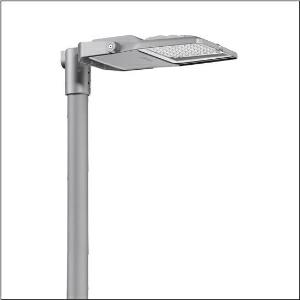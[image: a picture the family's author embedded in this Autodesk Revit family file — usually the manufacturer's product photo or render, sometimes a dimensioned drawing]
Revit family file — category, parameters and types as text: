
# Revit family: floodlight_fl_21_mini___pl61_5xa7776c2c3a_9e20
name_source: partatom
category: Lighting Fixtures
units: mm (PartAtom-declared; Revit-internal decimal feet)

## family parameters
Cut with Voids When Loaded = No
Host = Face
Light Source = No
Part Type = Normal
Room Calculation Point = No
Round Connector Dimension = Use Diameter
Shared = No

## types (1)
- --- (1 x LED, 11960 lm, 89 W, 3000K)
    Apparent Load = 89 VA
    CIE Flux Codes = 33 65 98 100 100
    Color Rendering = 70
    Color Temperature = 3000K
    Default Elevation = 1800 mm
    Description = Floodlight FL 21 mini, floodlight, primary light control with lens, of PMMA, primary optical cover: protective disc, of toughened safety glass, transparent, light distribution: PL61, light emission: direct distribution, installation type: surface-mounted, LED, High Power LED, rated luminous flux: 11.960lm, luminous efficacy: 134lm/W, light colour: 730, colour temperature: 3000K, control: flexible luminous flux parameterisation, time-dependent luminous flux control, constant luminous flux control, overheat protection, presetting dimming logarithmic, with terminal, 6-pole, mains connection: 220..240V, AC, 50/60Hz, start of lifetime: 89W, end of service life: 94W, reduction: 43W, luminaire housing, of diecast aluminium, powder-coated, Siteco® metallic grey (DB 702S), corrosivity category C5 mid according to DIN EN ISO 12944, sealing non-destructively replaceable, please order mast flange separately, mast bracket, of steel, galvanised, powder-coated, Siteco® metallic grey (DB 702S), Smart Interface below and above, protection rating (complete): IP66, insulation class (complete): insulation class II (safety insulation), certification: CE, ENEC, VDE, protection symbol: D, impact resistance: IK08, permissible operating ambient temperature: -40..+40°C, permissible operating ambient temperature for outdoor applications: -40..+50°C, standard: DIN EN 12944, LABS conformity tested according to VDMA 24364:2018-05, packaging unit: 1 piece

Light Distribution: PL61
    Height = 70 mm
    Lamp = 1 x LED
    Lamp Light Flux = 11960 lm
    Lamp Power = 89 W
    Lamp count = 1
    Length = 485 mm
    Luminous efficacy = 134 lm/W
    Manufacturer = Siteco
    ModVariant = No
    Model = 5XA7776C2C3A
    Number of Poles = 1
    OnlyDefault = Yes
    Power Factor = 1
    Product Name = Floodlight FL 21 mini | PL61
    Product group = floodlight | pylon annexe
    ProductGroupID = 6200
    Protection Class = Protection class II
    Protection Degree = IP 66
    RLX_Detail_Level = 1
    RLX_Emergency_Light_Flux = 0 lm
    RLX_Emergency_Type = 0
    RLX_Emergency_Type_DB = No
    RlxData = <blob elided: 100921 chars, md5=c063887c>
    Socket = socket
    Standby Power = 0 W
    System Light Flux = 11960 lm
    System Power = 89 W
    Type Comments = factory setting: luminous flux: 100 % | dim-lin: 254 | 456 mA
    Type Image = l_1007125.jpg
    URL = http://relux.com
    VarID = @adj_122925
    Voltage = 0 V
    Weight = 0.00 kg
    Width = 337 mm

## geometry (parser evidence)
native form markers: Blend x4, Sweep x16
no freeform markers — native parametric forms only
